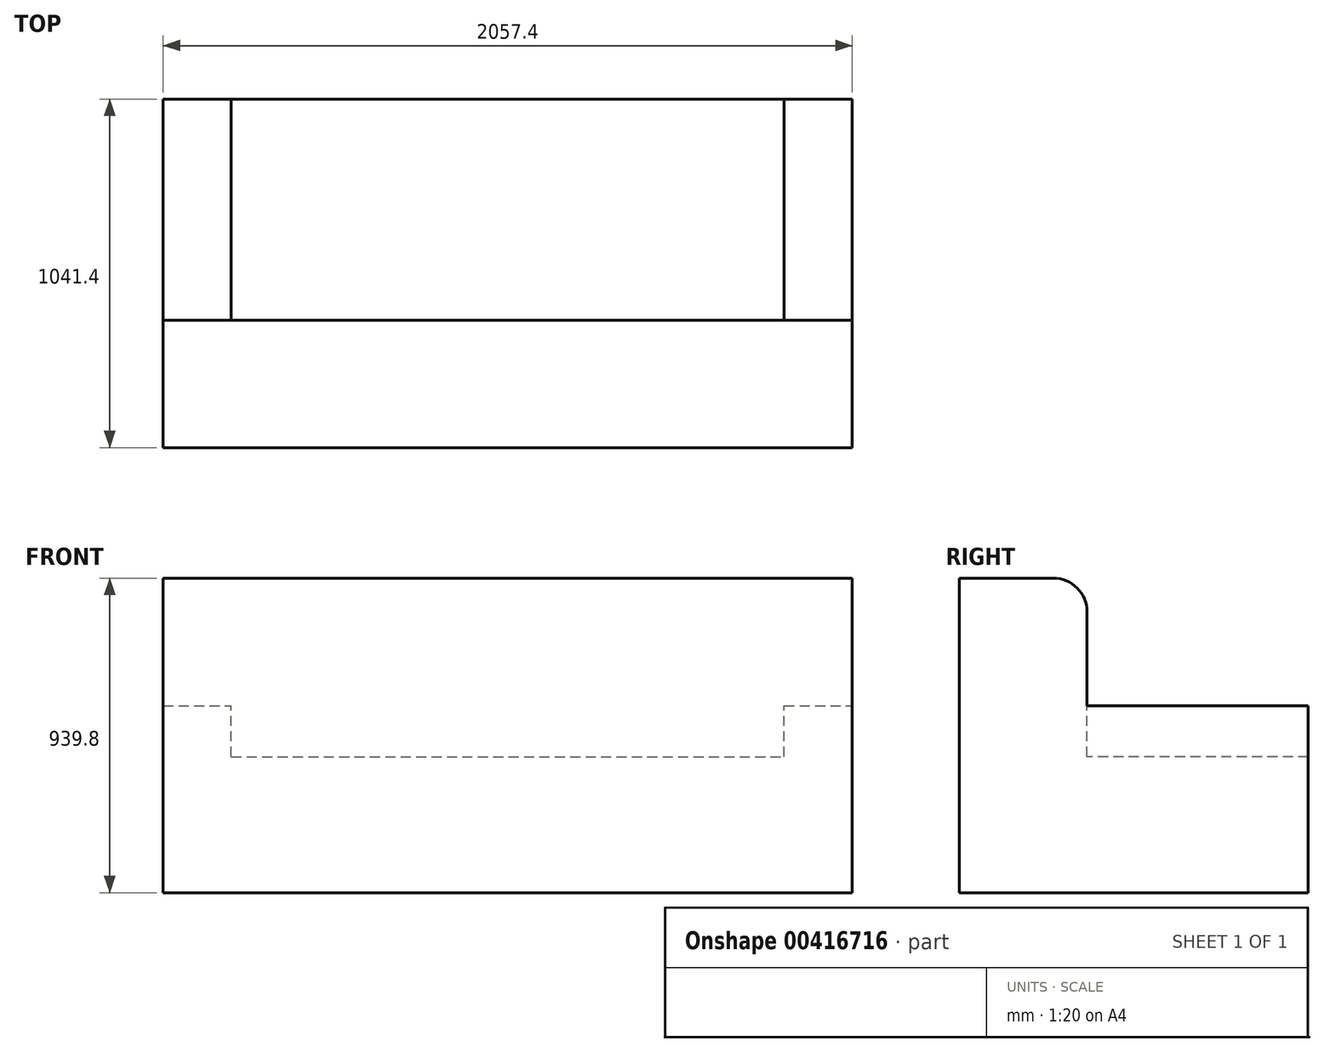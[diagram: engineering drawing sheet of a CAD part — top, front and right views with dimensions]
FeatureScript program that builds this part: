
annotation { "Feature Type Name" : "Feature", "Feature Type Description" : "" }
export const myFeature = defineFeature(function(context is Context, id is Id, definition is map)
    precondition{}
    {
        {
            var Q0;
            Q0=qCreatedBy(makeId("Right.planeOp"),FACE);
            var sketch = newSketch(context, id + "F0", { "sketchPlane" : qUnion([Q0])});
            skLineSegment(sketch, "E0", {"start": v(0, 0) * mm, "end": v(0, 939.8) * mm});
            skLineSegment(sketch, "E1", {"start": v(0, 939.8) * mm, "end": v(381, 939.8) * mm});
            skLineSegment(sketch, "E2", {"start": v(381, 939.8) * mm, "end": v(381, 558.8) * mm});
            skLineSegment(sketch, "E3", {"start": v(381, 558.8) * mm, "end": v(1041.4, 558.8) * mm});
            skLineSegment(sketch, "E4", {"start": v(1041.4, 558.8) * mm, "end": v(1041.4, 0) * mm});
            skLineSegment(sketch, "E5", {"start": v(1041.4, 0) * mm, "end": v(0, 0) * mm});
            skSolve(sketch);
        }
        {
            var Q0;
            Q0=makeQuery(id+"F0.imprint","IMPRINT",FACE,{"disambiguationData":[TD([[makeQuery(id+"F0.imprint","IMPRINT",EDGE,{"derivedFrom":sQuery(id+"F0.wireOp",EDGE,"E0")}),-1.0]])]});
            extrude(context, id + "F1", {"entities" : qUnion([Q0]), "flatOperationType" : FlatOperationType.REMOVE, "oppositeDirection" : true, "offsetDistance" : 25.4 * mm, "depth" : 2057.4 * mm, "domain" : OperationDomain.MODEL});
        }
        {
            var Q0;
            Q0=makeQuery(id+"F1.opExtrude","SWEPT_FACE",FACE,{"disambiguationData":[OSD([sQuery(id+"F0.wireOp",EDGE,"E3")])]});
            var sketch = newSketch(context, id + "F2", { "sketchPlane" : qUnion([Q0])});
            skLineSegment(sketch, "E6.bottom", {"start": v(-1854.2, 1041.4) * mm, "end": v(-203.2, 1041.4) * mm});
            skLineSegment(sketch, "E6.top", {"start": v(-1854.2, 381) * mm, "end": v(-203.2, 381) * mm});
            skLineSegment(sketch, "E6.left", {"start": v(-1854.2, 1041.4) * mm, "end": v(-1854.2, 381) * mm});
            skLineSegment(sketch, "E6.right", {"start": v(-203.2, 1041.4) * mm, "end": v(-203.2, 381) * mm});
            skLineSegment(sketch, "E7", {"start": v(-1854.2, 711.2) * mm, "end": v(-2057.4, 711.2) * mm, "construction": true});
            skLineSegment(sketch, "E8", {"start": v(-203.2, 711.2) * mm, "end": v(0, 711.2) * mm, "construction": true});
            skSolve(sketch);
        }
        {
            var Q0;
            Q0=makeQuery(id+"F2.imprint","IMPRINT",FACE,{"disambiguationData":[TD([[makeQuery(id+"F2.imprint","IMPRINT",EDGE,{"derivedFrom":sQuery(id+"F2.wireOp",EDGE,"E6.bottom")}),-1.0]])]});
            extrude(context, id + "F3", {"entities" : qUnion([Q0]), "operationType" : NewBodyOperationType.REMOVE, "oppositeDirection" : true, "depth" : 152.4 * mm});
        }
        {
            var Q0;
            Q0=makeQuery(id+"F3.boolean.opBoolean","COPY",EDGE,{"derivedFrom":makeQuery(id+"F3.opExtrude","CAP_EDGE",EDGE,{"disambiguationData":[OSD([sQuery(id+"F2.wireOp",EDGE,"E6.bottom")])],"isStart":false})});
            var Q1;
            Q1=makeQuery(id+"F1.opExtrude","SWEPT_EDGE",EDGE,{"disambiguationData":[OSD([sQuery(id+"F0.wireOp",EDGE,"E1"),sQuery(id+"F0.wireOp",EDGE,"E2")])]});
            var Q2;
            Q2=makeQuery(id+"F3.boolean.opBoolean","COPY",EDGE,{"derivedFrom":makeQuery(id+"F3.opExtrude","CAP_EDGE",EDGE,{"disambiguationData":[OSD([sQuery(id+"F2.wireOp",EDGE,"E6.right")])],"isStart":true})});
            var Q3;
            Q3=makeQuery(id+"F3.boolean.opBoolean","COPY",EDGE,{"derivedFrom":makeQuery(id+"F3.opExtrude","CAP_EDGE",EDGE,{"disambiguationData":[OSD([sQuery(id+"F2.wireOp",EDGE,"E6.left")])],"isStart":true})});
            fillet(context, id + "F4", {"entities" : qUnion([Q0, Q1, Q2, Q3]), "radius" : 101.6 * mm, "tangentPropagation" : true, "allowEdgeOverflow" : false});
        }
    });
